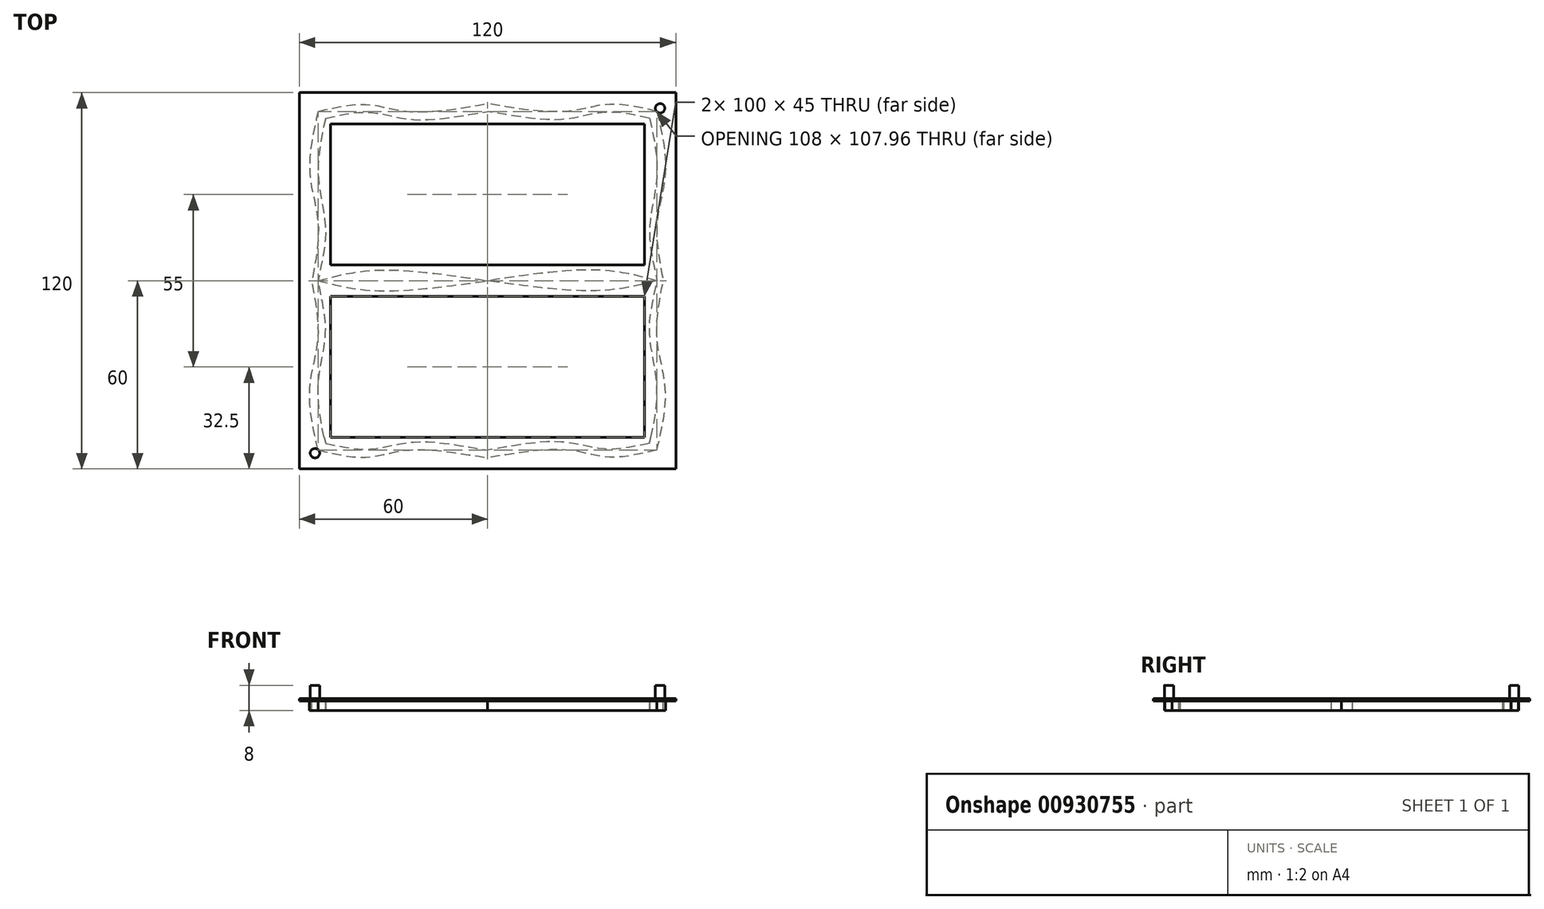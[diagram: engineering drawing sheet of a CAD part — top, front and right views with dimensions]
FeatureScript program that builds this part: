
annotation { "Feature Type Name" : "Feature", "Feature Type Description" : "" }
export const myFeature = defineFeature(function(context is Context, id is Id, definition is map)
    precondition{}
    {
        {
            var Q0;
            Q0=qCreatedBy(makeId("Top.planeOp"),FACE);
            var sketch = newSketch(context, id + "F0", { "sketchPlane" : qUnion([Q0])});
            skLineSegment(sketch, "E0.bottom", {"start": v(-60, 60) * mm, "end": v(60, 60) * mm});
            skLineSegment(sketch, "E0.top", {"start": v(-60, -60) * mm, "end": v(60, -60) * mm});
            skLineSegment(sketch, "E0.left", {"start": v(-60, 60) * mm, "end": v(-60, -60) * mm});
            skLineSegment(sketch, "E0.right", {"start": v(60, 60) * mm, "end": v(60, -60) * mm});
            skPoint(sketch, "E0.middle", {"position": v(0, 0) * mm});
            skSolve(sketch);
        }
        {
            var Q0;
            Q0=makeQuery(id+"F0.imprint","IMPRINT",FACE,{"disambiguationData":[TD([[makeQuery(id+"F0.imprint","IMPRINT",EDGE,{"derivedFrom":sQuery(id+"F0.wireOp",EDGE,"E0.bottom")}),-1.0]])]});
            extrude(context, id + "F1", {"entities" : qUnion([Q0]), "depth" : 5 * mm, "offsetDistance" : 25 * mm});
        }
        {
            var Q0;
            Q0=makeQuery(id+"F1.opExtrude","CAP_FACE",FACE,{"disambiguationData":[OSD([sQuery(id+"F0.wireOp",EDGE,"E0.bottom"),sQuery(id+"F0.wireOp",EDGE,"E0.top"),sQuery(id+"F0.wireOp",EDGE,"E0.left"),sQuery(id+"F0.wireOp",EDGE,"E0.right")])],"isStart":false});
            var sketch = newSketch(context, id + "F2", { "sketchPlane" : qUnion([Q0])});
            skLineSegment(sketch, "E1.bottom", {"start": v(-50, 50) * mm, "end": v(50, 50) * mm});
            skLineSegment(sketch, "E1.top", {"start": v(-50, -50) * mm, "end": v(50, -50) * mm});
            skLineSegment(sketch, "E1.left", {"start": v(-50, 50) * mm, "end": v(-50, -50) * mm});
            skLineSegment(sketch, "E1.right", {"start": v(50, 50) * mm, "end": v(50, -50) * mm});
            skPoint(sketch, "E1.middle", {"position": v(0, 0) * mm});
            skSolve(sketch);
        }
        {
            var Q0;
            Q0=makeQuery(id+"F2.imprint","IMPRINT",FACE,{"disambiguationData":[TD([[makeQuery(id+"F2.imprint","IMPRINT",EDGE,{"derivedFrom":sQuery(id+"F2.wireOp",EDGE,"E1.bottom")}),-1.0]])]});
            extrude(context, id + "F3", {"entities" : qUnion([Q0]), "operationType" : NewBodyOperationType.REMOVE, "oppositeDirection" : true, "depth" : 5 * mm, "offsetDistance" : 25 * mm});
        }
        {
            var Q0;
            Q0=makeQuery(id+"F1.opExtrude","CAP_FACE",FACE,{"disambiguationData":[OSD([sQuery(id+"F0.wireOp",EDGE,"E0.bottom"),sQuery(id+"F0.wireOp",EDGE,"E0.top"),sQuery(id+"F0.wireOp",EDGE,"E0.left"),sQuery(id+"F0.wireOp",EDGE,"E0.right")])],"isStart":false});
            var sketch = newSketch(context, id + "F4", { "sketchPlane" : qUnion([Q0])});
            skLineSegment(sketch, "E2.bottom", {"start": v(-50, -5) * mm, "end": v(50, -5) * mm});
            skLineSegment(sketch, "E2.top", {"start": v(-50, 5) * mm, "end": v(50, 5) * mm});
            skLineSegment(sketch, "E2.left", {"start": v(-50, -5) * mm, "end": v(-50, 5) * mm});
            skLineSegment(sketch, "E2.right", {"start": v(50, -5) * mm, "end": v(50, 5) * mm});
            skPoint(sketch, "E2.middle", {"position": v(0, 0) * mm});
            skSolve(sketch);
        }
        {
            var Q0;
            Q0 = qSketchRegion(id + "F4", true);
            extrude(context, id + "F5", {"entities" : qUnion([Q0]), "operationType" : NewBodyOperationType.ADD, "depth" : -5 * mm, "offsetDistance" : 25 * mm});
        }
        {
            var Q0;
            Q0=makeQuery(id+"F5.opExtrude","SWEPT_FACE",FACE,{"disambiguationData":[OSD([sQuery(id+"F4.wireOp",EDGE,"E2.top")])]});
            var sketch = newSketch(context, id + "F6", { "sketchPlane" : qUnion([Q0])});
            skLineSegment(sketch, "E3", {"start": v(0, 2) * mm, "end": v(0, 0) * mm});
            skLineSegment(sketch, "E4.bottom", {"start": v(50, 1) * mm, "end": v(-50, 1) * mm});
            skLineSegment(sketch, "E4.top", {"start": v(50, 3) * mm, "end": v(-50, 3) * mm});
            skLineSegment(sketch, "E4.left", {"start": v(50, 1) * mm, "end": v(50, 3) * mm});
            skLineSegment(sketch, "E4.right", {"start": v(-50, 1) * mm, "end": v(-50, 3) * mm});
            skPoint(sketch, "E4.middle", {"position": v(0, 2) * mm});
            skPoint(sketch, "E4.cornerSnap0", {"position": v(0, 1) * mm});
            skSolve(sketch);
        }
        {
            var Q0;
            Q0=makeQuery(id+"F6.imprint","IMPRINT",FACE,{"disambiguationData":[TD([[makeQuery(id+"F6.imprint","IMPRINT",EDGE,{"derivedFrom":sQuery(id+"F6.wireOp",EDGE,"E4.top")}),1.0]])]});
            extrude(context, id + "F7", {"entities" : qUnion([Q0]), "operationType" : NewBodyOperationType.REMOVE, "oppositeDirection" : true, "depth" : 2 * mm, "offsetDistance" : 25 * mm});
        }
        {
            var Q0;
            Q0=makeQuery(id+"F3.boolean.opBoolean","COPY",FACE,{"derivedFrom":makeQuery(id+"F3.opExtrude","SWEPT_FACE",FACE,{"disambiguationData":[OSD([sQuery(id+"F2.wireOp",EDGE,"E1.bottom")])]})});
            var sketch = newSketch(context, id + "F8", { "sketchPlane" : qUnion([Q0])});
            skLineSegment(sketch, "E5", {"start": v(0, 2) * mm, "end": v(0, 0) * mm});
            skLineSegment(sketch, "E6.bottom", {"start": v(50, 1) * mm, "end": v(-50, 1) * mm});
            skLineSegment(sketch, "E6.top", {"start": v(50, 3) * mm, "end": v(-50, 3) * mm});
            skLineSegment(sketch, "E6.left", {"start": v(50, 1) * mm, "end": v(50, 3) * mm});
            skLineSegment(sketch, "E6.right", {"start": v(-50, 1) * mm, "end": v(-50, 3) * mm});
            skPoint(sketch, "E6.middle", {"position": v(0, 2) * mm});
            skPoint(sketch, "E6.cornerSnap0", {"position": v(0, 1) * mm});
            skSolve(sketch);
        }
        {
            var Q0;
            Q0=makeQuery(id+"F8.imprint","IMPRINT",FACE,{"disambiguationData":[TD([[makeQuery(id+"F8.imprint","IMPRINT",EDGE,{"derivedFrom":sQuery(id+"F8.wireOp",EDGE,"E6.top")}),1.0]])]});
            extrude(context, id + "F9", {"entities" : qUnion([Q0]), "operationType" : NewBodyOperationType.REMOVE, "oppositeDirection" : true, "depth" : 2 * mm, "offsetDistance" : 25 * mm});
        }
        {
            var Q0;
            Q0=makeQuery(id+"F5.opExtrude","SWEPT_FACE",FACE,{"disambiguationData":[OSD([sQuery(id+"F4.wireOp",EDGE,"E2.bottom")])]});
            var sketch = newSketch(context, id + "F10", { "sketchPlane" : qUnion([Q0])});
            skLineSegment(sketch, "E7", {"start": v(0, 2) * mm, "end": v(0, 0) * mm});
            skLineSegment(sketch, "E8.bottom", {"start": v(50, 1) * mm, "end": v(-50, 1) * mm});
            skLineSegment(sketch, "E8.top", {"start": v(50, 3) * mm, "end": v(-50, 3) * mm});
            skLineSegment(sketch, "E8.left", {"start": v(50, 1) * mm, "end": v(50, 3) * mm});
            skLineSegment(sketch, "E8.right", {"start": v(-50, 1) * mm, "end": v(-50, 3) * mm});
            skPoint(sketch, "E8.middle", {"position": v(0, 2) * mm});
            skPoint(sketch, "E8.cornerSnap0", {"position": v(0, 1) * mm});
            skSolve(sketch);
        }
        {
            var Q0;
            Q0=makeQuery(id+"F10.imprint","IMPRINT",FACE,{"disambiguationData":[TD([[makeQuery(id+"F10.imprint","IMPRINT",EDGE,{"derivedFrom":sQuery(id+"F10.wireOp",EDGE,"E8.top")}),1.0]])]});
            extrude(context, id + "F11", {"entities" : qUnion([Q0]), "operationType" : NewBodyOperationType.REMOVE, "oppositeDirection" : true, "depth" : 2 * mm, "offsetDistance" : 25 * mm});
        }
        {
            var Q0;
            Q0=makeQuery(id+"F3.boolean.opBoolean","COPY",FACE,{"derivedFrom":makeQuery(id+"F3.opExtrude","SWEPT_FACE",FACE,{"disambiguationData":[OSD([sQuery(id+"F2.wireOp",EDGE,"E1.top")])]})});
            var sketch = newSketch(context, id + "F12", { "sketchPlane" : qUnion([Q0])});
            skLineSegment(sketch, "E9", {"start": v(0, 2) * mm, "end": v(0, 0) * mm});
            skLineSegment(sketch, "E10.bottom", {"start": v(50, 1) * mm, "end": v(-50, 1) * mm});
            skLineSegment(sketch, "E10.top", {"start": v(50, 3) * mm, "end": v(-50, 3) * mm});
            skLineSegment(sketch, "E10.left", {"start": v(50, 1) * mm, "end": v(50, 3) * mm});
            skLineSegment(sketch, "E10.right", {"start": v(-50, 1) * mm, "end": v(-50, 3) * mm});
            skPoint(sketch, "E10.middle", {"position": v(0, 2) * mm});
            skPoint(sketch, "E10.cornerSnap0", {"position": v(0, 1) * mm});
            skSolve(sketch);
        }
        {
            var Q0;
            Q0=makeQuery(id+"F12.imprint","IMPRINT",FACE,{"disambiguationData":[TD([[makeQuery(id+"F12.imprint","IMPRINT",EDGE,{"derivedFrom":sQuery(id+"F12.wireOp",EDGE,"E10.top")}),1.0]])]});
            extrude(context, id + "F13", {"entities" : qUnion([Q0]), "operationType" : NewBodyOperationType.REMOVE, "oppositeDirection" : true, "depth" : 2 * mm, "offsetDistance" : 25 * mm});
        }
        {
            var Q0;
            Q0=makeQuery(id+"F5.boolean.opBoolean","MERGE",FACE,{"derivedFrom":[makeQuery(id+"F1.opExtrude","CAP_FACE",FACE,{"disambiguationData":[OSD([sQuery(id+"F0.wireOp",EDGE,"E0.bottom"),sQuery(id+"F0.wireOp",EDGE,"E0.top"),sQuery(id+"F0.wireOp",EDGE,"E0.left"),sQuery(id+"F0.wireOp",EDGE,"E0.right")])],"isStart":false}),makeQuery(id+"F5.opExtrude","CAP_FACE",FACE,{"disambiguationData":[OSD([sQuery(id+"F4.wireOp",EDGE,"E2.bottom"),sQuery(id+"F4.wireOp",EDGE,"E2.top"),sQuery(id+"F4.wireOp",EDGE,"E2.left"),sQuery(id+"F4.wireOp",EDGE,"E2.right")])],"isStart":true})]});
            var sketch = newSketch(context, id + "F14", { "sketchPlane" : qUnion([Q0])});
            skLineSegment(sketch, "E11", {"start": v(-60, 60) * mm, "end": v(-55, 60) * mm});
            skLineSegment(sketch, "E12", {"start": v(-55, 60) * mm, "end": v(-55, 55) * mm});
            skCircle(sketch, "E13", {"center": v(-55, 55) * mm, "radius": 1.5 * mm});
            skCircle(sketch, "E14.MirrorC", {"center": v(55, 55) * mm, "radius": 1.5 * mm});
            skCircle(sketch, "E15.MirrorC", {"center": v(-55, -55) * mm, "radius": 1.5 * mm});
            skCircle(sketch, "E16.MirrorC", {"center": v(55, -55) * mm, "radius": 1.5 * mm});
            skSolve(sketch);
        }
        {
            var Q0;
            Q0=makeQuery(id+"F14.imprint","IMPRINT",FACE,{"disambiguationData":[TD([[makeQuery(id+"F14.imprint","IMPRINT",EDGE,{"derivedFrom":sQuery(id+"F14.wireOp",EDGE,"E13")}),1.0]])]});
            var Q1;
            Q1=makeQuery(id+"F14.imprint","IMPRINT",FACE,{"disambiguationData":[TD([[makeQuery(id+"F14.imprint","IMPRINT",EDGE,{"derivedFrom":sQuery(id+"F14.wireOp",EDGE,"E14.MirrorC")}),-1.0]])]});
            var Q2;
            Q2=makeQuery(id+"F14.imprint","IMPRINT",FACE,{"disambiguationData":[TD([[makeQuery(id+"F14.imprint","IMPRINT",EDGE,{"derivedFrom":sQuery(id+"F14.wireOp",EDGE,"E15.MirrorC")}),-1.0]])]});
            var Q3;
            Q3=makeQuery(id+"F14.imprint","IMPRINT",FACE,{"disambiguationData":[TD([[makeQuery(id+"F14.imprint","IMPRINT",EDGE,{"derivedFrom":sQuery(id+"F14.wireOp",EDGE,"E16.MirrorC")}),1.0]])]});
            extrude(context, id + "F15", {"entities" : qUnion([Q0, Q1, Q2, Q3]), "operationType" : NewBodyOperationType.REMOVE, "oppositeDirection" : true, "depth" : 4.25 * mm, "offsetDistance" : 25 * mm});
        }
        {
            var Q0;
            Q0=makeQuery(id+"F5.boolean.opBoolean","MERGE",FACE,{"derivedFrom":[makeQuery(id+"F1.opExtrude","CAP_FACE",FACE,{"disambiguationData":[OSD([sQuery(id+"F0.wireOp",EDGE,"E0.bottom"),sQuery(id+"F0.wireOp",EDGE,"E0.top"),sQuery(id+"F0.wireOp",EDGE,"E0.left"),sQuery(id+"F0.wireOp",EDGE,"E0.right")])],"isStart":true}),makeQuery(id+"F5.opExtrude","CAP_FACE",FACE,{"disambiguationData":[OSD([sQuery(id+"F4.wireOp",EDGE,"E2.bottom"),sQuery(id+"F4.wireOp",EDGE,"E2.top"),sQuery(id+"F4.wireOp",EDGE,"E2.left"),sQuery(id+"F4.wireOp",EDGE,"E2.right")])],"isStart":false})]});
            var sketch = newSketch(context, id + "F16", { "sketchPlane" : qUnion([Q0])});
            skLineSegment(sketch, "E17", {"start": v(-50, 50) * mm, "end": v(-54, 50) * mm});
            skLineSegment(sketch, "E18", {"start": v(-54, 50) * mm, "end": v(-54, 54) * mm});
            skLineSegment(sketch, "E19.MirrorCS", {"start": v(50, 50) * mm, "end": v(54, 50) * mm});
            skLineSegment(sketch, "E20.MirrorCS", {"start": v(54, 50) * mm, "end": v(54, 54) * mm});
            skFitSpline(sketch, "E21", {"points": [v(-54, 54) * mm, v(-38.61, 56.24) * mm, v(-25.12, 54) * mm, v(0, 56.46) * mm], "startDerivative": vector(51.28, 12.02) * mm, "endDerivative": vector(68.77, 11.5) * mm});
            skFitSpline(sketch, "E22.MirrorCS", {"points": [v(54, 54) * mm, v(38.61, 56.24) * mm, v(25.12, 54) * mm, v(0, 56.46) * mm], "startDerivative": vector(-51.28, 12.02) * mm, "endDerivative": vector(-68.77, 11.5) * mm});
            skFitSpline(sketch, "E23.MirrorCS", {"points": [v(-54, -54) * mm, v(-38.61, -56.24) * mm, v(-25.12, -54) * mm, v(0, -56.46) * mm], "startDerivative": vector(51.28, -12.02) * mm, "endDerivative": vector(68.77, -11.5) * mm});
            skFitSpline(sketch, "E24.MirrorCS", {"points": [v(54, -54) * mm, v(38.61, -56.24) * mm, v(25.12, -54) * mm, v(0, -56.46) * mm], "startDerivative": vector(-51.28, -12.02) * mm, "endDerivative": vector(-68.77, -11.5) * mm});
            skFitSpline(sketch, "E25", {"points": [v(-54, 54) * mm, v(-56.69, 34.58) * mm, v(-54, 18.39) * mm, v(-56.01, 0) * mm], "startDerivative": vector(-13.22, -57.68) * mm, "endDerivative": vector(-10.99, -55.94) * mm});
            skFitSpline(sketch, "E26.MirrorCS", {"points": [v(54, 54) * mm, v(56.69, 34.58) * mm, v(54, 18.39) * mm, v(56.01, 0) * mm], "startDerivative": vector(13.22, -57.68) * mm, "endDerivative": vector(10.99, -55.94) * mm});
            skFitSpline(sketch, "E27.MirrorCS", {"points": [v(-54, -54) * mm, v(-56.69, -34.58) * mm, v(-54, -18.39) * mm, v(-56.01, 0) * mm], "startDerivative": vector(-13.22, 57.68) * mm, "endDerivative": vector(-10.99, 55.94) * mm});
            skFitSpline(sketch, "E28.MirrorCS", {"points": [v(54, -54) * mm, v(56.69, -34.58) * mm, v(54, -18.39) * mm, v(56.01, 0) * mm], "startDerivative": vector(13.22, 57.68) * mm, "endDerivative": vector(10.99, 55.94) * mm});
            skFitSpline(sketch, "E29", {"points": [v(-51.61, 51.82) * mm, v(-37.11, 53.66) * mm, v(-23.62, 51.43) * mm, v(0, 53.98) * mm], "startDerivative": vector(51.28, 12.02) * mm, "endDerivative": vector(68.77, 11.5) * mm});
            skFitSpline(sketch, "E30.MirrorCS", {"points": [v(51.61, 51.82) * mm, v(37.11, 53.66) * mm, v(23.62, 51.43) * mm, v(0, 53.98) * mm], "startDerivative": vector(-51.28, 12.02) * mm, "endDerivative": vector(-68.77, 11.5) * mm});
            skFitSpline(sketch, "E31", {"points": [v(-51.61, 51.82) * mm, v(-53.92, 32.7) * mm, v(-51.63, 16.4) * mm, v(-54, 0) * mm], "startDerivative": vector(-13.8, -57.55) * mm, "endDerivative": vector(-10.6, -56) * mm});
            skFitSpline(sketch, "E32.MirrorCS", {"points": [v(51.61, 51.82) * mm, v(53.92, 32.7) * mm, v(51.63, 16.4) * mm, v(54, 0) * mm], "startDerivative": vector(13.8, -57.55) * mm, "endDerivative": vector(10.6, -56) * mm});
            skFitSpline(sketch, "E33.MirrorCS", {"points": [v(-51.61, -51.82) * mm, v(-53.92, -32.7) * mm, v(-51.63, -16.4) * mm, v(-54, 0) * mm], "startDerivative": vector(-13.8, 57.55) * mm, "endDerivative": vector(-10.6, 56) * mm});
            skFitSpline(sketch, "E34.MirrorCS", {"points": [v(-51.61, -51.82) * mm, v(-37.11, -53.66) * mm, v(-23.62, -51.43) * mm, v(0, -53.98) * mm], "startDerivative": vector(51.28, -12.02) * mm, "endDerivative": vector(68.77, -11.5) * mm});
            skFitSpline(sketch, "E35.MirrorCS", {"points": [v(51.61, -51.82) * mm, v(37.11, -53.66) * mm, v(23.62, -51.43) * mm, v(0, -53.98) * mm], "startDerivative": vector(-51.28, -12.02) * mm, "endDerivative": vector(-68.77, -11.5) * mm});
            skFitSpline(sketch, "E36.MirrorCS", {"points": [v(51.61, -51.82) * mm, v(53.92, -32.7) * mm, v(51.63, -16.4) * mm, v(54, 0) * mm], "startDerivative": vector(13.8, 57.55) * mm, "endDerivative": vector(10.6, 56) * mm});
            skFitSpline(sketch, "E37", {"points": [v(-54, 0) * mm, v(-35.2, 3.16) * mm, v(0, 0) * mm], "startDerivative": vector(40.87, 10.21) * mm, "endDerivative": vector(65.85, -9.22) * mm});
            skFitSpline(sketch, "E38", {"points": [v(-54, 0) * mm, v(-35.2, -3.39) * mm, v(0, 0) * mm], "startDerivative": vector(40.84, -10.94) * mm, "endDerivative": vector(65.88, 9.88) * mm});
            skFitSpline(sketch, "E39.MirrorCS", {"points": [v(54, 0) * mm, v(35.2, 3.16) * mm, v(0, 0) * mm], "startDerivative": vector(-40.87, 10.21) * mm, "endDerivative": vector(-65.85, -9.22) * mm});
            skFitSpline(sketch, "E40.MirrorCS", {"points": [v(54, 0) * mm, v(35.2, -3.39) * mm, v(0, 0) * mm], "startDerivative": vector(-40.84, -10.94) * mm, "endDerivative": vector(-65.88, 9.88) * mm});
            skSolve(sketch);
        }
        {
            var Q0;
            {var subQ0=sQuery(id+"F16.wireOp",EDGE,"E18");Q0=makeQuery(id+"F16.imprint","IMPRINT",FACE,{"disambiguationData":[TD([[makeQuery(id+"F16.imprint","IMPRINT",EDGE,{"derivedFrom":subQ0}),1.0]])]});}
            var Q1;
            {var subQ9=sQuery(id+"F16.wireOp",EDGE,"E18");Q1=makeQuery(id+"F16.imprint","IMPRINT",FACE,{"disambiguationData":[TD([[makeQuery(id+"F16.imprint","IMPRINT",EDGE,{"derivedFrom":subQ9}),-1.0]])]});}
            var Q2;
            Q2=makeQuery(id+"F16.imprint","IMPRINT",FACE,{"disambiguationData":[TD([[makeQuery(id+"F16.imprint","IMPRINT",EDGE,{"derivedFrom":sQuery(id+"F16.wireOp",EDGE,"E39.MirrorCS")}),1.0]])]});
            var Q3;
            Q3=makeQuery(id+"F16.imprint","IMPRINT",FACE,{"disambiguationData":[TD([[makeQuery(id+"F16.imprint","IMPRINT",EDGE,{"derivedFrom":sQuery(id+"F16.wireOp",EDGE,"E37")}),-1.0]])]});
            extrude(context, id + "F17", {"entities" : qUnion([Q0, Q1, Q2, Q3]), "depth" : 3 * mm, "offsetDistance" : 25 * mm});
        }
    });
